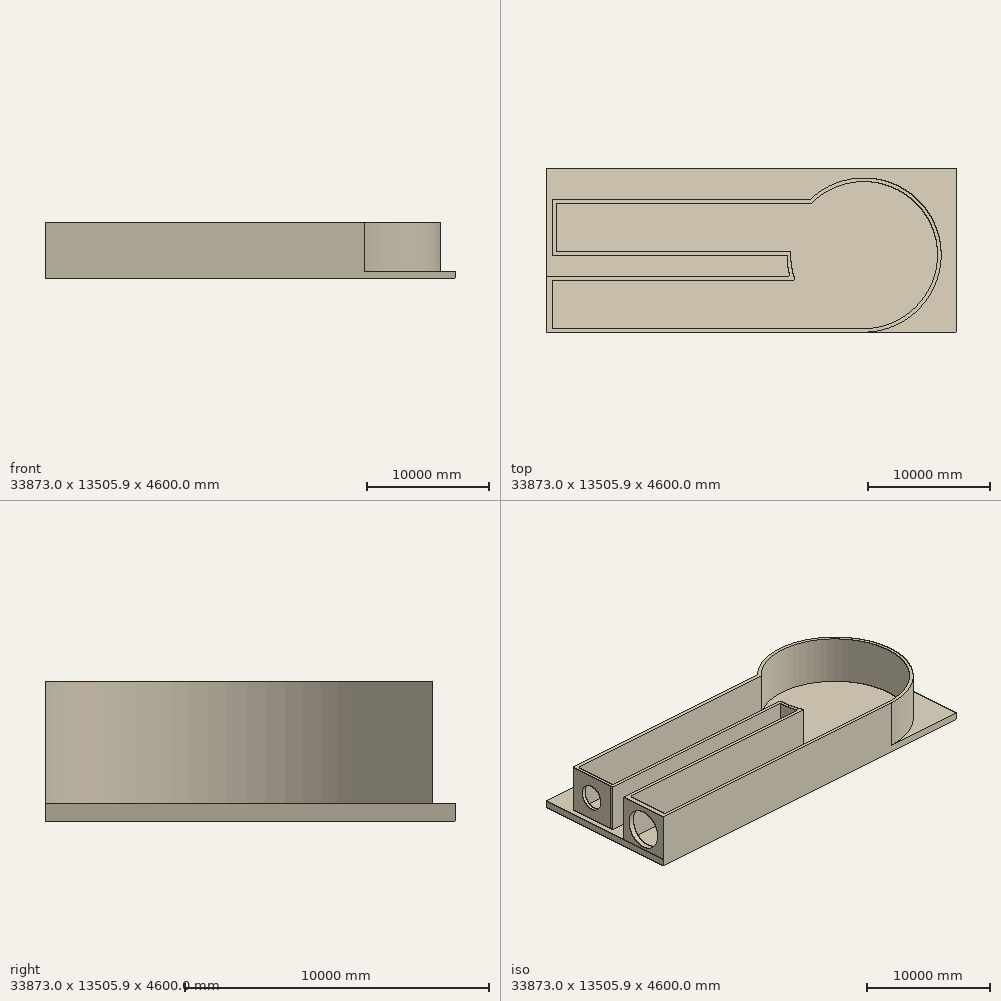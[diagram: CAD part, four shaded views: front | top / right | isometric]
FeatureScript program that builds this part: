
annotation { "Feature Type Name" : "Feature", "Feature Type Description" : "" }
export const myFeature = defineFeature(function(context is Context, id is Id, definition is map)
    precondition{}
    {
        {
            var Q0;
            Q0=qCreatedBy(makeId("Top.planeOp"),FACE);
            var sketch = newSketch(context, id + "F0", { "sketchPlane" : qUnion([Q0])});
            skLineSegment(sketch, "E0", {"start": v(-357.01, -1.8) * mm, "end": v(-19699.05, -1.8) * mm});
            skLineSegment(sketch, "E1.0", {"start": v(1415.12, 3998.2) * mm, "end": v(-19699.05, 3998.2) * mm});
            skLineSegment(sketch, "E2.0", {"start": v(1292.64, 4298.2) * mm, "end": v(-19999.05, 4298.2) * mm});
            skLineSegment(sketch, "E3.0", {"start": v(-664.14, -301.8) * mm, "end": v(-20000, -301.8) * mm});
            skArc(sketch, "E4", {"start": v(-357.01, -1.8) * mm, "mid": v(-296.17, -1202.04) * mm, "end": v(-0.13, -2366.78) * mm});
            skArc(sketch, "E5.0", {"start": v(-664.14, -301.8) * mm, "mid": v(-600.68, -1193.11) * mm, "end": v(-413.16, -2066.78) * mm});
            skLineSegment(sketch, "E6", {"start": v(5818.93, -6666.78) * mm, "end": v(-20531.78, -6666.78) * mm});
            skLineSegment(sketch, "E7.0", {"start": v(5819, -6366.78) * mm, "end": v(-20031.76, -6366.78) * mm});
            skLineSegment(sketch, "E8.0", {"start": v(-0.13, -2366.78) * mm, "end": v(-20031.43, -2366.78) * mm});
            skLineSegment(sketch, "E9.0", {"start": v(-413.16, -2066.78) * mm, "end": v(-20531.41, -2066.78) * mm});
            skArc(sketch, "E10.trimOffspring", {"start": v(5598.82, -6366.78) * mm, "mid": v(11337.89, 1976.57) * mm, "end": v(1415.12, 3998.2) * mm});
            skArc(sketch, "E11.trimOffspring", {"start": v(5596.17, -6666.78) * mm, "mid": v(11638.78, 2031.83) * mm, "end": v(1292.64, 4298.2) * mm});
            skLineSegment(sketch, "E12", {"start": v(-20531.41, -2066.78) * mm, "end": v(-20531.78, -6666.78) * mm});
            skLineSegment(sketch, "E13.0", {"start": v(-20031.43, -2366.78) * mm, "end": v(-20031.76, -6366.78) * mm});
            skLineSegment(sketch, "E14.trimOffspring", {"start": v(-20531.43, -2366.78) * mm, "end": v(-20531.53, -2366.78) * mm});
            skLineSegment(sketch, "E15.trimOffspring", {"start": v(-20031.78, -6666.78) * mm, "end": v(-20031.78, -6666.83) * mm});
            skLineSegment(sketch, "E16", {"start": v(-19999.05, 3998.2) * mm, "end": v(-19999.05, 4298.2) * mm});
            skLineSegment(sketch, "E17", {"start": v(-19999.05, -1.8) * mm, "end": v(-20000, -301.8) * mm});
            skLineSegment(sketch, "E18", {"start": v(-19999.05, 3998.2) * mm, "end": v(-19999.05, -1.8) * mm});
            skLineSegment(sketch, "E19.0", {"start": v(-19699.05, 3998.2) * mm, "end": v(-19699.05, -1.8) * mm});
            skSolve(sketch);
        }
        {
            var Q0;
            {var subQ0=sQuery(id+"F0.wireOp",EDGE,"E11.trimOffspring");var subQ1=sQuery(id+"F0.wireOp",EDGE,"E6");var subQ2=makeQuery(id+"F0.imprint","INTERSECT",VERTEX,{"disambiguationData":[OD(0.0)],"derivedFrom":[subQ1,subQ0]});Q0=makeQuery(id+"F0.imprint","IMPRINT",FACE,{"disambiguationData":[TD([[makeQuery(id+"F0.imprint","IMPRINT",EDGE,{"disambiguationData":[TD([[subQ2,-1.0]])],"derivedFrom":subQ1}),1.0]])]});}
            var Q1;
            {var subQ0=sQuery(id+"F0.wireOp",EDGE,"E10.trimOffspring");var subQ1=sQuery(id+"F0.wireOp",EDGE,"E7.0");var subQ2=makeQuery(id+"F0.imprint","INTERSECT",VERTEX,{"disambiguationData":[OD(0.0)],"derivedFrom":[subQ1,subQ0]});Q1=makeQuery(id+"F0.imprint","IMPRINT",FACE,{"disambiguationData":[TD([[makeQuery(id+"F0.imprint","IMPRINT",EDGE,{"disambiguationData":[TD([[subQ2,1.0]])],"derivedFrom":subQ1}),1.0]])]});}
            var Q2;
            Q2=makeQuery(id+"F0.imprint","IMPRINT",FACE,{"disambiguationData":[TD([[makeQuery(id+"F0.imprint","IMPRINT",EDGE,{"derivedFrom":sQuery(id+"F0.wireOp",EDGE,"E0")}),1.0]])]});
            extrude(context, id + "F1", {"entities" : qUnion([Q0, Q1, Q2]), "depth" : 4000 * mm});
        }
        {
            var Q0;
            Q0=makeQuery(id+"F1.opExtrude","CAP_FACE",FACE,{"disambiguationData":[OSD([sQuery(id+"F0.wireOp",EDGE,"E0"),sQuery(id+"F0.wireOp",EDGE,"E1.0"),sQuery(id+"F0.wireOp",EDGE,"E2.0"),sQuery(id+"F0.wireOp",EDGE,"E3.0"),sQuery(id+"F0.wireOp",EDGE,"E4"),sQuery(id+"F0.wireOp",EDGE,"E5.0"),sQuery(id+"F0.wireOp",EDGE,"E6"),sQuery(id+"F0.wireOp",EDGE,"E7.0"),sQuery(id+"F0.wireOp",EDGE,"E8.0"),sQuery(id+"F0.wireOp",EDGE,"E9.0"),sQuery(id+"F0.wireOp",EDGE,"E10.trimOffspring"),sQuery(id+"F0.wireOp",EDGE,"E11.trimOffspring"),sQuery(id+"F0.wireOp",EDGE,"E12"),sQuery(id+"F0.wireOp",EDGE,"E13.0"),sQuery(id+"F0.wireOp",EDGE,"E16"),sQuery(id+"F0.wireOp",EDGE,"E17")])],"isStart":true});
            var sketch = newSketch(context, id + "F2", { "sketchPlane" : qUnion([Q0])});
            skLineSegment(sketch, "E20.bottom", {"start": v(-20531.78, 6666.78) * mm, "end": v(13341.22, 6666.78) * mm});
            skLineSegment(sketch, "E20.top", {"start": v(-20531.78, -6839.15) * mm, "end": v(13341.22, -6839.15) * mm});
            skLineSegment(sketch, "E20.left", {"start": v(-20531.78, 6666.78) * mm, "end": v(-20531.78, -6839.15) * mm});
            skLineSegment(sketch, "E20.right", {"start": v(13341.22, 6666.78) * mm, "end": v(13341.22, -6839.15) * mm});
            skSolve(sketch);
        }
        {
            var Q0;
            Q0 = qSketchRegion(id + "F2", true);
            extrude(context, id + "F3", {"entities" : qUnion([Q0]), "operationType" : NewBodyOperationType.ADD, "depth" : 600 * mm});
        }
        {
            var Q0;
            Q0=makeQuery(id+"F1.opExtrude","SWEPT_FACE",FACE,{"disambiguationData":[OSD([sQuery(id+"F0.wireOp",EDGE,"E12")])]});
            var sketch = newSketch(context, id + "F4", { "sketchPlane" : qUnion([Q0])});
            skPoint(sketch, "E21.centerSnap0", {"position": v(4368.45, 0) * mm});
            skCircle(sketch, "E22", {"center": v(4368.45, 1896.98) * mm, "radius": 1652.83 * mm});
            skSolve(sketch);
        }
        {
            var Q0;
            Q0 = qSketchRegion(id + "F4", true);
            extrude(context, id + "F5", {"entities" : qUnion([Q0]), "operationType" : NewBodyOperationType.REMOVE, "oppositeDirection" : true, "depth" : 500 * mm});
        }
        {
            var Q0;
            Q0=makeQuery(id+"F1.opExtrude","SWEPT_FACE",FACE,{"disambiguationData":[OSD([sQuery(id+"F0.wireOp",EDGE,"E16"),sQuery(id+"F0.wireOp",EDGE,"E18")])]});
            var sketch = newSketch(context, id + "F6", { "sketchPlane" : qUnion([Q0])});
            skCircle(sketch, "E23", {"center": v(-2148.2, 2000) * mm, "radius": 1070.22 * mm});
            skPoint(sketch, "E23.centerSnap0", {"position": v(-4298.2, 2000) * mm});
            skPoint(sketch, "E23.centerSnap1", {"position": v(-2148.2, 0) * mm});
            skSolve(sketch);
        }
        {
            var Q0;
            Q0 = qSketchRegion(id + "F6", true);
            extrude(context, id + "F7", {"entities" : qUnion([Q0]), "operationType" : NewBodyOperationType.REMOVE, "oppositeDirection" : true, "depth" : 350 * mm});
        }
    });
